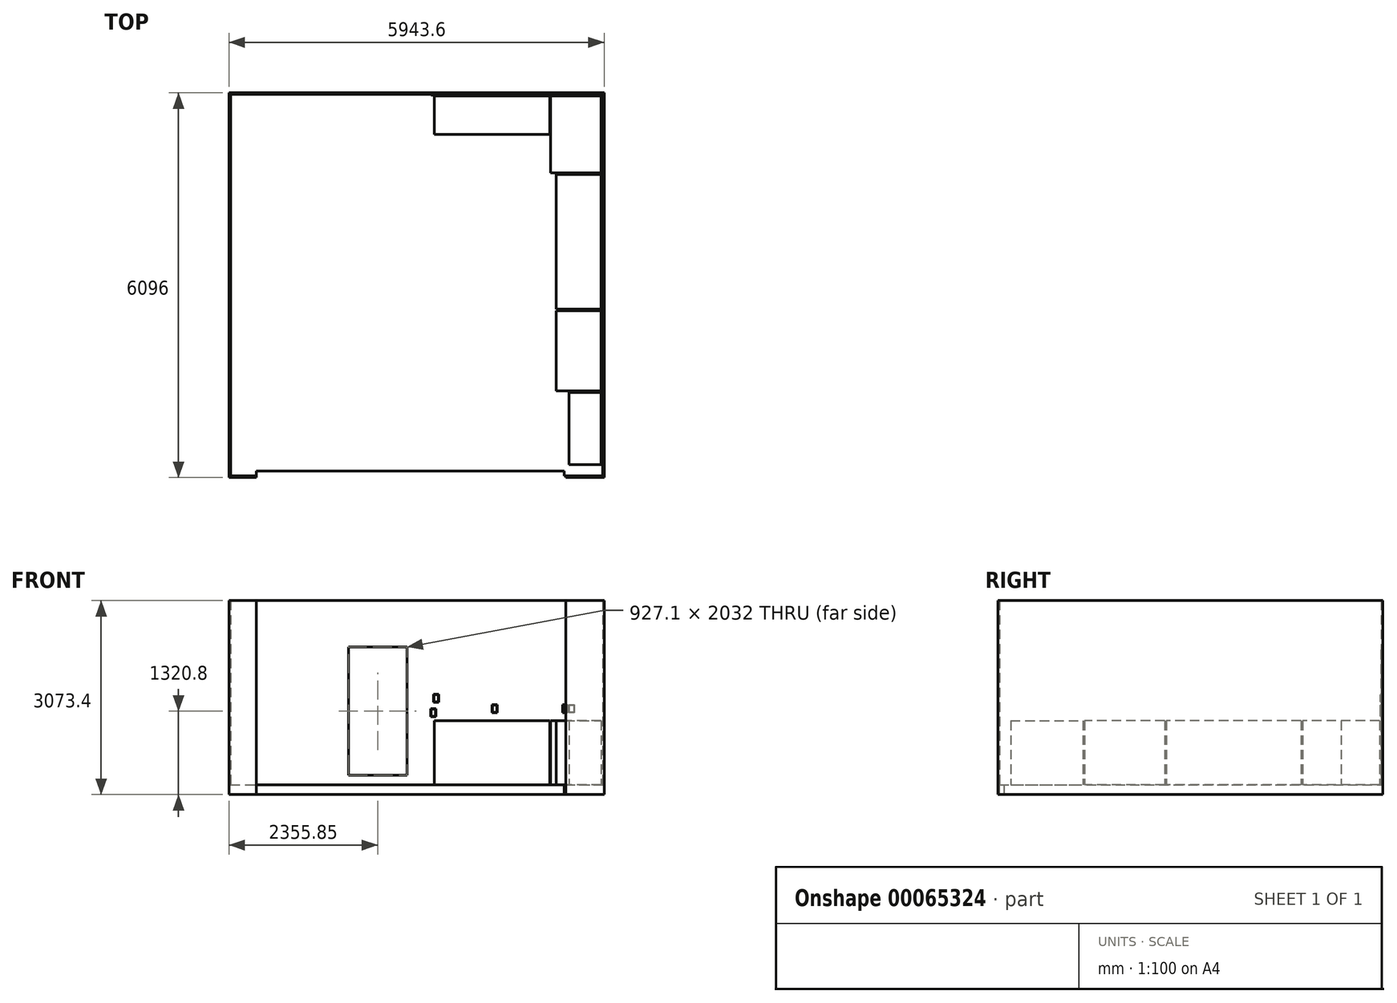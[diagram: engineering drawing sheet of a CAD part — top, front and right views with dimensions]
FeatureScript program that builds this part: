
annotation { "Feature Type Name" : "Feature", "Feature Type Description" : "" }
export const myFeature = defineFeature(function(context is Context, id is Id, definition is map)
    precondition{}
    {
        {
            var Q0;
            Q0=qCreatedBy(makeId("Top.planeOp"),FACE);
            var sketch = newSketch(context, id + "F0", { "sketchPlane" : qUnion([Q0])});
            skLineSegment(sketch, "E0.bottom", {"start": v(0, 0) * mm, "end": v(406.4, 0) * mm});
            skLineSegment(sketch, "E0.top", {"start": v(0, 6045.2) * mm, "end": v(5892.8, 6045.2) * mm});
            skLineSegment(sketch, "E0.left", {"start": v(0, 0) * mm, "end": v(0, 6045.2) * mm});
            skLineSegment(sketch, "E0.right", {"start": v(5892.8, 0) * mm, "end": v(5892.8, 6045.2) * mm});
            skLineSegment(sketch, "E1", {"start": v(406.4, 0) * mm, "end": v(406.4, 76.2) * mm});
            skLineSegment(sketch, "E2", {"start": v(406.4, 76.2) * mm, "end": v(5283.2, 76.2) * mm});
            skLineSegment(sketch, "E3", {"start": v(5283.2, 76.2) * mm, "end": v(5283.2, 0) * mm});
            skLineSegment(sketch, "E4.trimOffspring", {"start": v(5283.2, 0) * mm, "end": v(5892.8, 0) * mm});
            skSolve(sketch);
        }
        {
            var Q0;
            Q0=makeQuery(id+"F0.imprint","IMPRINT",FACE,{"disambiguationData":[TD([[makeQuery(id+"F0.imprint","IMPRINT",EDGE,{"derivedFrom":sQuery(id+"F0.wireOp",EDGE,"E0.bottom")}),1.0]])]});
            extrude(context, id + "F1", {"entities" : qUnion([Q0]), "oppositeDirection" : true, "depth" : 152.4 * mm});
        }
        {
            var Q0;
            Q0=qCreatedBy(makeId("Top.planeOp"),FACE);
            var sketch = newSketch(context, id + "F2", { "sketchPlane" : qUnion([Q0])});
            skLineSegment(sketch, "E5.0", {"start": v(0, 0) * mm, "end": v(0, 6045.2) * mm});
            skLineSegment(sketch, "E6.0", {"start": v(0, 6045.2) * mm, "end": v(5892.8, 6045.2) * mm});
            skLineSegment(sketch, "E7.0", {"start": v(5892.8, 0) * mm, "end": v(5892.8, 6045.2) * mm});
            skLineSegment(sketch, "E8.0", {"start": v(-25.4, 6070.6) * mm, "end": v(5918.2, 6070.6) * mm});
            skLineSegment(sketch, "E9.0", {"start": v(5918.2, -25.4) * mm, "end": v(5918.2, 6070.6) * mm});
            skLineSegment(sketch, "E10.0", {"start": v(-25.4, -25.4) * mm, "end": v(-25.4, 6070.6) * mm});
            skLineSegment(sketch, "E11", {"start": v(0, 0) * mm, "end": v(406.4, 0) * mm});
            skLineSegment(sketch, "E12", {"start": v(406.4, 0) * mm, "end": v(406.4, -25.4) * mm});
            skLineSegment(sketch, "E13", {"start": v(406.4, -25.4) * mm, "end": v(-25.4, -25.4) * mm});
            skLineSegment(sketch, "E14", {"start": v(5892.8, 0) * mm, "end": v(5308.6, 0) * mm});
            skLineSegment(sketch, "E15", {"start": v(5308.6, 0) * mm, "end": v(5308.6, -25.4) * mm});
            skLineSegment(sketch, "E16", {"start": v(5308.6, -25.4) * mm, "end": v(5918.2, -25.4) * mm});
            skLineSegment(sketch, "E17", {"start": v(406.4, -25.4) * mm, "end": v(5308.6, -25.4) * mm, "construction": true});
            skSolve(sketch);
        }
        {
            var Q0;
            Q0 = qSketchRegion(id + "F2", true);
            extrude(context, id + "F3", {"entities" : qUnion([Q0]), "operationType" : NewBodyOperationType.ADD, "depth" : 2921 * mm, "hasSecondDirection" : true, "secondDirectionOppositeDirection" : true, "secondDirectionDepth" : 152.4 * mm});
        }
        {
            var Q0;
            Q0=makeQuery(id+"F3.opExtrude","SWEPT_FACE",FACE,{"disambiguationData":[OSD([sQuery(id+"F2.wireOp",EDGE,"E6.0")])]});
            var sketch = newSketch(context, id + "F4", { "sketchPlane" : qUnion([Q0])});
            skLineSegment(sketch, "E18.bottom", {"start": v(1866.9, 152.4) * mm, "end": v(2794, 152.4) * mm});
            skLineSegment(sketch, "E18.top", {"start": v(1866.9, 2184.4) * mm, "end": v(2794, 2184.4) * mm});
            skLineSegment(sketch, "E18.left", {"start": v(1866.9, 152.4) * mm, "end": v(1866.9, 2184.4) * mm});
            skLineSegment(sketch, "E18.right", {"start": v(2794, 152.4) * mm, "end": v(2794, 2184.4) * mm});
            skSolve(sketch);
        }
        {
            var Q0;
            Q0 = qSketchRegion(id + "F4", true);
            extrude(context, id + "F5", {"entities" : qUnion([Q0]), "operationType" : NewBodyOperationType.REMOVE, "oppositeDirection" : true, "depth" : 25.4 * mm});
        }
        {
            var Q0;
            Q0=makeQuery(id+"F3.opExtrude","SWEPT_FACE",FACE,{"disambiguationData":[OSD([sQuery(id+"F2.wireOp",EDGE,"E6.0")])]});
            var sketch = newSketch(context, id + "F6", { "sketchPlane" : qUnion([Q0])});
            skLineSegment(sketch, "E19.bottom", {"start": v(3171.19, 1206.5) * mm, "end": v(3253.74, 1206.5) * mm});
            skLineSegment(sketch, "E19.top", {"start": v(3171.19, 1079.5) * mm, "end": v(3253.74, 1079.5) * mm});
            skLineSegment(sketch, "E19.left", {"start": v(3171.19, 1206.5) * mm, "end": v(3171.19, 1079.5) * mm});
            skLineSegment(sketch, "E19.right", {"start": v(3253.74, 1206.5) * mm, "end": v(3253.74, 1079.5) * mm});
            skLineSegment(sketch, "E20.bottom", {"start": v(4140.2, 1270) * mm, "end": v(4222.75, 1270) * mm});
            skLineSegment(sketch, "E20.top", {"start": v(4140.2, 1143) * mm, "end": v(4222.75, 1143) * mm});
            skLineSegment(sketch, "E20.left", {"start": v(4140.2, 1270) * mm, "end": v(4140.2, 1143) * mm});
            skLineSegment(sketch, "E20.right", {"start": v(4222.75, 1270) * mm, "end": v(4222.75, 1143) * mm});
            skLineSegment(sketch, "E21.bottom", {"start": v(3215.64, 1435.1) * mm, "end": v(3298.19, 1435.1) * mm});
            skLineSegment(sketch, "E21.top", {"start": v(3215.64, 1308.1) * mm, "end": v(3298.19, 1308.1) * mm});
            skLineSegment(sketch, "E21.left", {"start": v(3215.64, 1435.1) * mm, "end": v(3215.64, 1308.1) * mm});
            skLineSegment(sketch, "E21.right", {"start": v(3298.19, 1435.1) * mm, "end": v(3298.19, 1308.1) * mm});
            skLineSegment(sketch, "E22.bottom", {"start": v(5359.4, 1270) * mm, "end": v(5441.95, 1270) * mm});
            skLineSegment(sketch, "E22.top", {"start": v(5359.4, 1143) * mm, "end": v(5441.95, 1143) * mm});
            skLineSegment(sketch, "E22.left", {"start": v(5359.4, 1270) * mm, "end": v(5359.4, 1143) * mm});
            skLineSegment(sketch, "E22.right", {"start": v(5441.95, 1270) * mm, "end": v(5441.95, 1143) * mm});
            skLineSegment(sketch, "E23.bottom", {"start": v(5257.8, 1270) * mm, "end": v(5340.35, 1270) * mm});
            skLineSegment(sketch, "E23.top", {"start": v(5257.8, 1143) * mm, "end": v(5340.35, 1143) * mm});
            skLineSegment(sketch, "E23.left", {"start": v(5257.8, 1270) * mm, "end": v(5257.8, 1143) * mm});
            skLineSegment(sketch, "E23.right", {"start": v(5340.35, 1270) * mm, "end": v(5340.35, 1143) * mm});
            skSolve(sketch);
        }
        {
            var Q0;
            Q0 = qSketchRegion(id + "F6", true);
            extrude(context, id + "F7", {"entities" : qUnion([Q0]), "operationType" : NewBodyOperationType.ADD, "depth" : 9.52 * mm, "hasDraft" : true, "draftAngle" : 35 * degree, "draftPullDirection" : true});
        }
        {
            var Q0;
            Q0=makeQuery(id+"F1.opExtrude","CAP_FACE",FACE,{"disambiguationData":[OSD([sQuery(id+"F0.wireOp",EDGE,"E0.bottom"),sQuery(id+"F0.wireOp",EDGE,"E0.top"),sQuery(id+"F0.wireOp",EDGE,"E0.left"),sQuery(id+"F0.wireOp",EDGE,"E0.right"),sQuery(id+"F0.wireOp",EDGE,"E1"),sQuery(id+"F0.wireOp",EDGE,"E2"),sQuery(id+"F0.wireOp",EDGE,"E3"),sQuery(id+"F0.wireOp",EDGE,"E4.trimOffspring")])],"isStart":true});
            var sketch = newSketch(context, id + "F8", { "sketchPlane" : qUnion([Q0])});
            skLineSegment(sketch, "E24.bottom", {"start": v(3225.8, 6019.8) * mm, "end": v(5054.6, 6019.8) * mm});
            skLineSegment(sketch, "E24.top", {"start": v(3225.8, 5410.2) * mm, "end": v(5054.6, 5410.2) * mm});
            skLineSegment(sketch, "E24.left", {"start": v(3225.8, 6019.8) * mm, "end": v(3225.8, 5410.2) * mm});
            skLineSegment(sketch, "E24.right", {"start": v(5054.6, 6019.8) * mm, "end": v(5054.6, 5410.2) * mm});
            skSolve(sketch);
        }
        {
            var Q0;
            Q0 = qSketchRegion(id + "F8", true);
            extrude(context, id + "F9", {"entities" : qUnion([Q0]), "offsetDistance" : 25.4 * mm, "depth" : 1016 * mm});
        }
        {
            var Q0;
            Q0=makeQuery(id+"F1.opExtrude","CAP_FACE",FACE,{"disambiguationData":[OSD([sQuery(id+"F0.wireOp",EDGE,"E0.bottom"),sQuery(id+"F0.wireOp",EDGE,"E0.top"),sQuery(id+"F0.wireOp",EDGE,"E0.left"),sQuery(id+"F0.wireOp",EDGE,"E0.right"),sQuery(id+"F0.wireOp",EDGE,"E1"),sQuery(id+"F0.wireOp",EDGE,"E2"),sQuery(id+"F0.wireOp",EDGE,"E3"),sQuery(id+"F0.wireOp",EDGE,"E4.trimOffspring")])],"isStart":true});
            var sketch = newSketch(context, id + "F10", { "sketchPlane" : qUnion([Q0])});
            skLineSegment(sketch, "E25.bottom", {"start": v(5067.3, 6019.8) * mm, "end": v(5867.4, 6019.8) * mm});
            skLineSegment(sketch, "E25.top", {"start": v(5067.3, 4800.6) * mm, "end": v(5867.4, 4800.6) * mm});
            skLineSegment(sketch, "E25.left", {"start": v(5067.3, 6019.8) * mm, "end": v(5067.3, 4800.6) * mm});
            skLineSegment(sketch, "E25.right", {"start": v(5867.4, 6019.8) * mm, "end": v(5867.4, 4800.6) * mm});
            skSolve(sketch);
        }
        {
            var Q0;
            Q0=makeQuery(id+"F10.imprint","IMPRINT",FACE,{"disambiguationData":[TD([[makeQuery(id+"F10.imprint","IMPRINT",EDGE,{"derivedFrom":sQuery(id+"F10.wireOp",EDGE,"E25.bottom")}),-1.0]])]});
            extrude(context, id + "F11", {"entities" : qUnion([Q0]), "depth" : 1016 * mm, "offsetDistance" : 25.4 * mm});
        }
        {
            var Q0;
            Q0=makeQuery(id+"F1.opExtrude","CAP_FACE",FACE,{"disambiguationData":[OSD([sQuery(id+"F0.wireOp",EDGE,"E0.bottom"),sQuery(id+"F0.wireOp",EDGE,"E0.top"),sQuery(id+"F0.wireOp",EDGE,"E0.left"),sQuery(id+"F0.wireOp",EDGE,"E0.right"),sQuery(id+"F0.wireOp",EDGE,"E1"),sQuery(id+"F0.wireOp",EDGE,"E2"),sQuery(id+"F0.wireOp",EDGE,"E3"),sQuery(id+"F0.wireOp",EDGE,"E4.trimOffspring")])],"isStart":true});
            var sketch = newSketch(context, id + "F12", { "sketchPlane" : qUnion([Q0])});
            skSolve(sketch);
        }
        {
            var Q0;
            {var subQ3=sQuery(id+"F0.wireOp",EDGE,"E1");Q0=makeQuery(id+"F12.imprint","IMPRINT",FACE,{"disambiguationData":[TD([[makeQuery(id+"F12.imprint","IMPRINT",EDGE,{"derivedFrom":makeQuery(id+"F1.opExtrude","CAP_EDGE",EDGE,{"disambiguationData":[OSD([subQ3])],"isStart":true})}),1.0]])]});}
            var sketch = newSketch(context, id + "F13", { "sketchPlane" : qUnion([Q0])});
            skLineSegment(sketch, "E26.bottom", {"start": v(5867.4, 4775.2) * mm, "end": v(5156.2, 4775.2) * mm});
            skLineSegment(sketch, "E26.top", {"start": v(5867.4, 2641.6) * mm, "end": v(5156.2, 2641.6) * mm});
            skLineSegment(sketch, "E26.left", {"start": v(5867.4, 4775.2) * mm, "end": v(5867.4, 2641.6) * mm});
            skLineSegment(sketch, "E26.right", {"start": v(5156.2, 4775.2) * mm, "end": v(5156.2, 2641.6) * mm});
            skSolve(sketch);
        }
        {
            var Q0;
            Q0 = qSketchRegion(id + "F13", true);
            extrude(context, id + "F14", {"entities" : qUnion([Q0]), "depth" : 1016 * mm, "offsetDistance" : 25.4 * mm});
        }
        {
            var Q0;
            {var subQ3=sQuery(id+"F0.wireOp",EDGE,"E1");Q0=makeQuery(id+"F12.imprint","IMPRINT",FACE,{"disambiguationData":[TD([[makeQuery(id+"F12.imprint","IMPRINT",EDGE,{"derivedFrom":makeQuery(id+"F1.opExtrude","CAP_EDGE",EDGE,{"disambiguationData":[OSD([subQ3])],"isStart":true})}),1.0]])]});}
            var sketch = newSketch(context, id + "F15", { "sketchPlane" : qUnion([Q0])});
            skLineSegment(sketch, "E27.bottom", {"start": v(5867.4, 2616.2) * mm, "end": v(5156.2, 2616.2) * mm});
            skLineSegment(sketch, "E27.top", {"start": v(5867.4, 1346.2) * mm, "end": v(5156.2, 1346.2) * mm});
            skLineSegment(sketch, "E27.left", {"start": v(5867.4, 2616.2) * mm, "end": v(5867.4, 1346.2) * mm});
            skLineSegment(sketch, "E27.right", {"start": v(5156.2, 2616.2) * mm, "end": v(5156.2, 1346.2) * mm});
            skSolve(sketch);
        }
        {
            var Q0;
            Q0 = qSketchRegion(id + "F15", true);
            extrude(context, id + "F16", {"entities" : qUnion([Q0]), "depth" : 1016 * mm, "offsetDistance" : 25.4 * mm});
        }
        {
            var Q0;
            Q0=makeQuery(id+"F13.imprint","IMPRINT",FACE,{"disambiguationData":[TD([[makeQuery(id+"F13.imprint","IMPRINT",EDGE,{"derivedFrom":sQuery(id+"F13.wireOp",EDGE,"E26.bottom")}),-1.0]])]});
            var sketch = newSketch(context, id + "F17", { "sketchPlane" : qUnion([Q0])});
            skLineSegment(sketch, "E28.bottom", {"start": v(5867.4, 177.8) * mm, "end": v(5359.4, 177.8) * mm});
            skLineSegment(sketch, "E28.top", {"start": v(5867.4, 1320.8) * mm, "end": v(5359.4, 1320.8) * mm});
            skLineSegment(sketch, "E28.left", {"start": v(5867.4, 177.8) * mm, "end": v(5867.4, 1320.8) * mm});
            skLineSegment(sketch, "E28.right", {"start": v(5359.4, 177.8) * mm, "end": v(5359.4, 1320.8) * mm});
            skSolve(sketch);
        }
        {
            var Q0;
            Q0 = qSketchRegion(id + "F17", true);
            extrude(context, id + "F18", {"entities" : qUnion([Q0]), "depth" : 1016 * mm, "offsetDistance" : 25.4 * mm});
        }
    });
